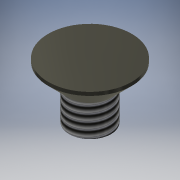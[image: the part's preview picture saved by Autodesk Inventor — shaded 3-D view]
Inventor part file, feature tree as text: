
AUTODESK INVENTOR PART (.ipt)
format: ipt  version: 2016 (Build 200138000, 138)  size: 128,512 bytes
history: native  units: mm
features: extrude x4, sketch x4, other x1, thread x1, chamfer x1
ambient origin geometry x1: Origin
bodies: Body1 (feature_tree)
feature tree (11):
  other  "ソリッド1"
  extrude  "押し出し1"  Depth=3.0mm
  extrude  "押し出し2"  Depth=6.0mm TaperAngle=0.0deg
  thread  "ねじ1"
  chamfer  "面取り1"  Distance=6.0mm
  extrude  "押し出し4"  Depth=1.75mm TaperAngle=0.0deg
  extrude  "押し出し5"  Depth=10.0mm TaperAngle=0.0deg
  sketch  "スケッチ1"
  sketch  "スケッチ2"
  sketch  "スケッチ4"
  sketch  "スケッチ5"
